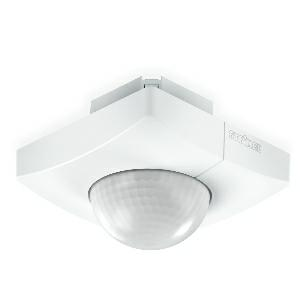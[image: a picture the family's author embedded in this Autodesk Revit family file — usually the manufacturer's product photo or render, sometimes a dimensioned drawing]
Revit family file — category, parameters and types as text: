
# Revit family: is_3360_033460
name_source: partatom
category: Elektroinstallationen
revit_build: Autodesk Revit 2016 (Build: 20190508_0715(x64)
units: mm (PartAtom-declared; Revit-internal decimal feet)

## family parameters
Basisbauteil = Fläche
Beim Laden mit Abzugskörper schneiden = Nein
Bemaßung runder Anschluss = Durchmesser verwenden
Beschriftungsausrichtung beibehalten = Nein
Gemeinsam genutzt = Nein
Raumberechnungspunkt = Nein
Teiletyp = Normal

## types (1)
- IS 3360
    Apparent Load = 0 VA
    Beschreibung = Type: Motion and Presence Detector; Dimensions (L x W x H): 78 x 94 x 94 mm; Mains power supply: 220 – 240 V / 50 – 60 Hz; Sensor Technology: passive infrared; Application, place: Indoors; Application, room: production facilities, recreation room, changing room, function room / ancillary room, sports hall, reception / lobby, stairwell, WC / washroom, multi-storey / underground car park, warehouse, Indoors; Installation site: ceiling; Installation: Concealed wiring; Switching zones: 1416 switching zones; Electronic scalability: No; Mechanical scalability: No; Mounting height: 2,50 – 4,00 m; Optimum mounting height: 2,8 m; Detection angle: 360 °; Angle of aperture: 180 °; Sneak-by guard: Yes; Capability of masking out individual segments: Yes; Reach, radial: Ø 8 m (50 m²); Reach, tangential: Ø 40 m (1257 m²); Reach, presence: Ø 3 m (7 m²); Twilight setting TEACH: Yes; Twilight setting: 2 – 1000 lx; Time setting: 5 sec – 15 min; Switching output 1, resistive: 2000 W; Switching output 1, number of LEDs / fluorescent lamps: 8 pcs.; Constant-lighting control: No; Basic light level function: No; Functions: Normal / test mode, Manual ON / ON-OFF; Settings via: Remote control, Potentiometers, Smart Remote; With remote control: No; Interconnection: Yes; IP-rating: IP20; Material: Plastic; Ambient temperature: -20 – 50 °C; Colour: white; Colour, RAL: 9003; Manufacturer's Warranty: 5 years; Version: COM1 - concealed, sq. white; PU1, EAN: 4007841033460
    Height = 0 mm  [stored 0 ft]
    Hersteller = Steinel
    Length = 78 mm  [stored 0.255906 ft]
    Maximum range = 20.158 m
    ModVariant = Nein
    Modell = 033460
    Mounting Place = Ceiling
    Mounting Type = Recessed
    Number of Poles = 1
    OnlyDefault = Ja
    Power Factor = 1
    Product Name = IS 3360
    Product group = Presence detector
    ProductGroupID = 4
    Protection Class = Protection class
    Protection Degree = IP 20
    RlxData = <blob elided: 159041 chars, md5=931b5cb3>
    Sensor characteristics = Circular 300°-360°
    Sensor type = Passive (infrared)
    SensorDataFile = <blob elided: 6785 chars, md5=23016e95>
    Type of entry = Presence, Motion
    Typenbild = produkt1_033460.jpg
    Typenkommentare = Product without accessories
    URL = http://relux.com
    VarID = ---
    Voltage = 0 V
    Vorgabe-Ansicht = 1800 mm
    Weight = 0.00 kg
    Width = 94 mm  [stored 0.308399 ft]

note: [stored X ft] marks values corroborated as IEEE doubles in the binary element streams (Revit-internal decimal feet)

## geometry (parser evidence)
native form markers: Blend x4, Sweep x18
no freeform markers — native parametric forms only
